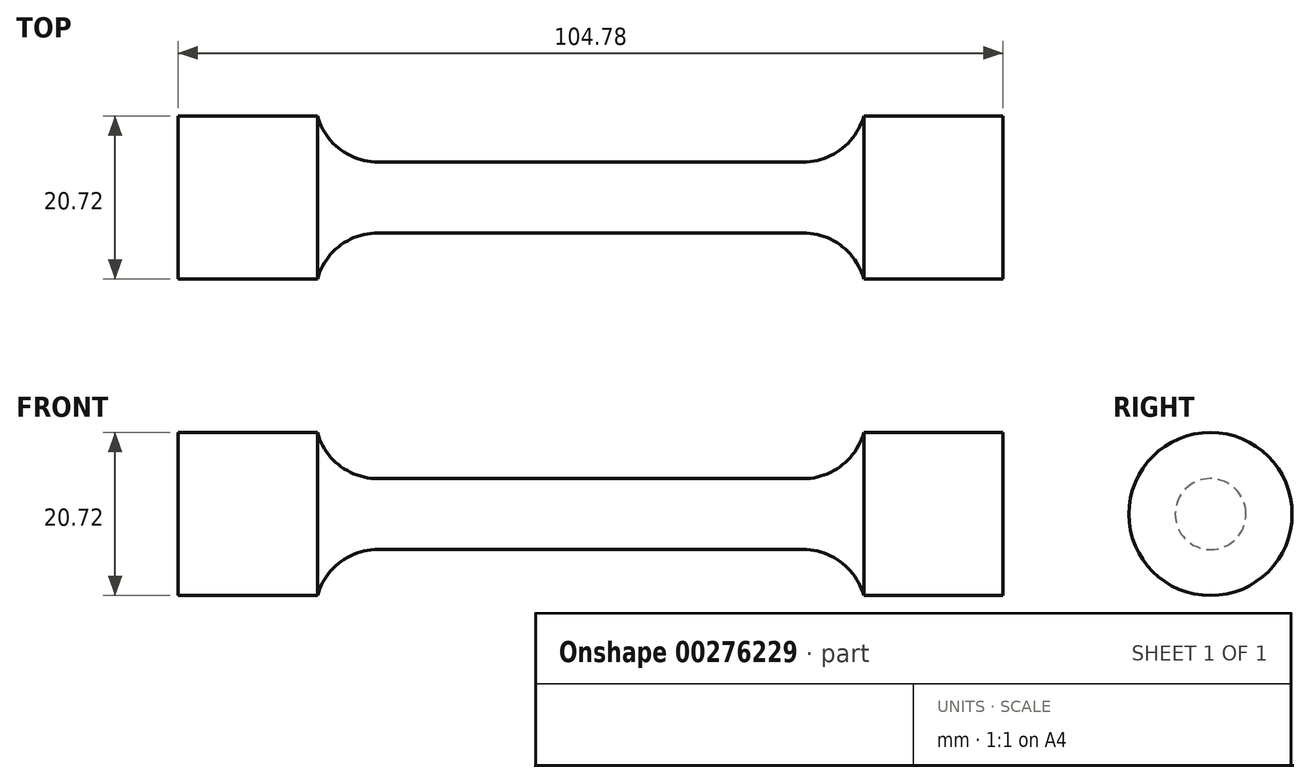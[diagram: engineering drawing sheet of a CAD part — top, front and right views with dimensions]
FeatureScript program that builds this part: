
annotation { "Feature Type Name" : "Feature", "Feature Type Description" : "" }
export const myFeature = defineFeature(function(context is Context, id is Id, definition is map)
    precondition{}
    {
        {
            var Q0;
            Q0=qCreatedBy(makeId("Front.planeOp"),FACE);
            var sketch = newSketch(context, id + "F0", { "sketchPlane" : qUnion([Q0])});
            skLineSegment(sketch, "E0", {"start": v(0, 4.5) * mm, "end": v(27, 4.5) * mm});
            skArc(sketch, "E1", {"start": v(27, 4.5) * mm, "mid": v(31.84, 6.13) * mm, "end": v(34.7, 10.36) * mm});
            skLineSegment(sketch, "E2", {"start": v(34.7, 10.36) * mm, "end": v(52.4, 10.36) * mm});
            skLineSegment(sketch, "E3", {"start": v(52.4, 10.36) * mm, "end": v(52.4, 0) * mm});
            skLineSegment(sketch, "E4", {"start": v(52.4, 0) * mm, "end": v(0, 0) * mm});
            skLineSegment(sketch, "E5.MirrorCS", {"start": v(0, 4.5) * mm, "end": v(-27, 4.5) * mm});
            skLineSegment(sketch, "E6.MirrorCS", {"start": v(-52.4, 0) * mm, "end": v(0, 0) * mm});
            skLineSegment(sketch, "E7.MirrorCS", {"start": v(-34.7, 10.36) * mm, "end": v(-52.4, 10.36) * mm});
            skLineSegment(sketch, "E8.MirrorCS", {"start": v(-52.4, 10.36) * mm, "end": v(-52.4, 0) * mm});
            skArc(sketch, "E9.MirrorCS", {"start": v(-27, 4.5) * mm, "mid": v(-31.84, 6.13) * mm, "end": v(-34.7, 10.36) * mm});
            skSolve(sketch);
        }
        {
            var Q0;
            Q0 = qSketchRegion(id + "F0", true);
            var Q1;
            Q1=sQuery(id+"F0.wireOp",EDGE,"E6.MirrorCS");
            revolve(context, id + "F1", {"entities" : qUnion([Q0]), "axis" : qUnion([Q1]), "revolveType" : RevolveType.FULL});
        }
    });
